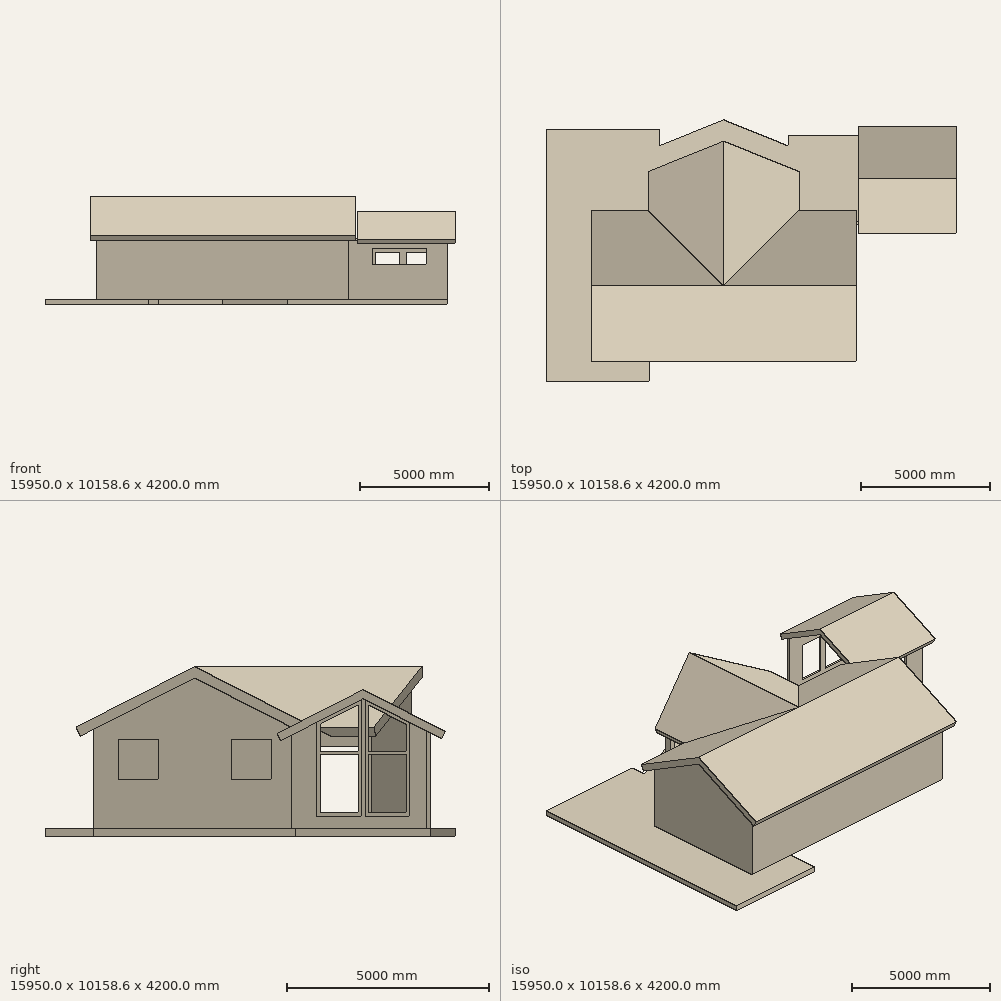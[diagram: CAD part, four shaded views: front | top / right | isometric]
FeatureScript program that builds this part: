
annotation { "Feature Type Name" : "Feature", "Feature Type Description" : "" }
export const myFeature = defineFeature(function(context is Context, id is Id, definition is map)
    precondition{}
    {
        {
            var Q0;
            Q0=qCreatedBy(makeId("Top.planeOp"),FACE);
            var sketch = newSketch(context, id + "F0", { "sketchPlane" : qUnion([Q0])});
            skLineSegment(sketch, "E0", {"start": v(-4900, 0) * mm, "end": v(-4900, 5000) * mm});
            skLineSegment(sketch, "E1", {"start": v(-4900, 5000) * mm, "end": v(-2500, 5000) * mm});
            skLineSegment(sketch, "E2", {"start": v(-2500, 5000) * mm, "end": v(-2500, 6870) * mm});
            skLineSegment(sketch, "E3", {"start": v(-2500, 6870) * mm, "end": v(0, 7880.07) * mm});
            skLineSegment(sketch, "E4", {"start": v(0, 7880.07) * mm, "end": v(2500, 6870) * mm});
            skLineSegment(sketch, "E5", {"start": v(2500, 6870) * mm, "end": v(2500, 5000) * mm});
            skLineSegment(sketch, "E6", {"start": v(2500, 5000) * mm, "end": v(4900, 5000) * mm});
            skLineSegment(sketch, "E7", {"start": v(4900, 5000) * mm, "end": v(4900, 0) * mm});
            skLineSegment(sketch, "E8", {"start": v(4900, 0) * mm, "end": v(-4900, 0) * mm});
            skLineSegment(sketch, "E9", {"start": v(0, 7880.07) * mm, "end": v(-2500, 7880.07) * mm, "construction": true});
            skLineSegment(sketch, "E10", {"start": v(-2500, 7880.07) * mm, "end": v(-2500, 6870) * mm, "construction": true});
            skSolve(sketch);
        }
        {
            var Q0;
            Q0=makeQuery(id+"F0.imprint","IMPRINT",FACE,{"disambiguationData":[TD([[makeQuery(id+"F0.imprint","IMPRINT",EDGE,{"derivedFrom":sQuery(id+"F0.wireOp",EDGE,"E0")}),-1.0]])]});
            extrude(context, id + "F1", {"entities" : qUnion([Q0]), "depth" : 4000 * mm, "offsetDistance" : 25 * mm});
        }
        {
            var Q0;
            Q0=makeQuery(id+"F1.opExtrude","SWEPT_FACE",FACE,{"disambiguationData":[OSD([sQuery(id+"F0.wireOp",EDGE,"E0")])]});
            var sketch = newSketch(context, id + "F2", { "sketchPlane" : qUnion([Q0])});
            skLineSegment(sketch, "E11", {"start": v(-5000, 2726.19) * mm, "end": v(-2500, 4000) * mm});
            skLineSegment(sketch, "E12", {"start": v(-2500, 4000) * mm, "end": v(0, 2726.19) * mm});
            skLineSegment(sketch, "E13", {"start": v(0, 2726.19) * mm, "end": v(0, 4000) * mm});
            skLineSegment(sketch, "E14", {"start": v(0, 4000) * mm, "end": v(-2500, 4000) * mm});
            skLineSegment(sketch, "E15", {"start": v(-5000, 4000) * mm, "end": v(-5000, 2726.19) * mm});
            skSolve(sketch);
        }
        {
            var Q0;
            {var subQ0=sQuery(id+"F2.wireOp",EDGE,"E11");Q0=makeQuery(id+"F2.imprint","IMPRINT",FACE,{"disambiguationData":[TD([[makeQuery(id+"F2.imprint","IMPRINT",EDGE,{"derivedFrom":subQ0}),1.0]])]});}
            var Q1;
            Q1=makeQuery(id+"F2.imprint","IMPRINT",FACE,{"disambiguationData":[TD([[makeQuery(id+"F2.imprint","IMPRINT",EDGE,{"derivedFrom":sQuery(id+"F2.wireOp",EDGE,"E12")}),1.0]])]});
            extrude(context, id + "F3", {"entities" : qUnion([Q0, Q1]), "operationType" : NewBodyOperationType.REMOVE, "endBound" : BoundingType.THROUGH_ALL, "oppositeDirection" : true, "depth" : 25 * mm, "offsetDistance" : 25 * mm});
        }
        {
            var Q0;
            Q0=makeQuery(id+"F3.boolean.opBoolean","COPY",FACE,{"derivedFrom":makeQuery(id+"F3.opExtrude","SWEPT_FACE",FACE,{"disambiguationData":[OSD([sQuery(id+"F2.wireOp",EDGE,"E15")])]})});
            var sketch = newSketch(context, id + "F4", { "sketchPlane" : qUnion([Q0])});
            skLineSegment(sketch, "E16", {"start": v(0, 4000) * mm, "end": v(-2500, 2726.19) * mm});
            skLineSegment(sketch, "E17", {"start": v(-2500, 2726.19) * mm, "end": v(-2500, 4000) * mm});
            skLineSegment(sketch, "E18", {"start": v(-2500, 4000) * mm, "end": v(2500, 4000) * mm});
            skLineSegment(sketch, "E19", {"start": v(2500, 4000) * mm, "end": v(2500, 2726.19) * mm});
            skLineSegment(sketch, "E20", {"start": v(2500, 2726.19) * mm, "end": v(0, 4000) * mm});
            skSolve(sketch);
        }
        {
            var Q0;
            Q0 = qSketchRegion(id + "F4", true);
            extrude(context, id + "F5", {"entities" : qUnion([Q0]), "operationType" : NewBodyOperationType.REMOVE, "endBound" : BoundingType.THROUGH_ALL, "oppositeDirection" : true, "depth" : 25 * mm, "offsetDistance" : 25 * mm});
        }
        {
            var Q0;
            Q0=makeQuery(id+"F1.opExtrude","SWEPT_FACE",FACE,{"disambiguationData":[OSD([sQuery(id+"F0.wireOp",EDGE,"E0")])]});
            var sketch = newSketch(context, id + "F6", { "sketchPlane" : qUnion([Q0])});
            skLineSegment(sketch, "E21", {"start": v(-2500, 4000) * mm, "end": v(-5445.5, 2499.2) * mm});
            skLineSegment(sketch, "E22", {"start": v(-5445.5, 2499.2) * mm, "end": v(-5332, 2276.44) * mm});
            skLineSegment(sketch, "E23", {"start": v(-5332, 2276.44) * mm, "end": v(-2500, 3719.42) * mm});
            skLineSegment(sketch, "E24", {"start": v(-2500, 3719.42) * mm, "end": v(332, 2276.44) * mm});
            skLineSegment(sketch, "E25", {"start": v(332, 2276.44) * mm, "end": v(445.5, 2499.2) * mm});
            skLineSegment(sketch, "E26", {"start": v(445.5, 2499.2) * mm, "end": v(-2500, 4000) * mm});
            skPoint(sketch, "E27", {"position": v(0, 2726.19) * mm});
            skSolve(sketch);
        }
        {
            var Q0;
            Q0 = qSketchRegion(id + "F6", true);
            extrude(context, id + "F7", {"entities" : qUnion([Q0]), "operationType" : NewBodyOperationType.ADD, "depth" : 250 * mm, "offsetDistance" : 25 * mm, "hasSecondDirection" : true, "secondDirectionOppositeDirection" : true, "secondDirectionDepth" : 10050 * mm});
        }
        {
            var Q0;
            Q0=makeQuery(id+"F3.boolean.opBoolean","COPY",FACE,{"derivedFrom":makeQuery(id+"F3.opExtrude","SWEPT_FACE",FACE,{"disambiguationData":[OSD([sQuery(id+"F2.wireOp",EDGE,"E15")])]})});
            var sketch = newSketch(context, id + "F8", { "sketchPlane" : qUnion([Q0])});
            skLineSegment(sketch, "E28", {"start": v(0, 4000) * mm, "end": v(-2945.5, 2499.2) * mm});
            skLineSegment(sketch, "E29", {"start": v(-2945.5, 2499.2) * mm, "end": v(-2832, 2276.44) * mm});
            skLineSegment(sketch, "E30", {"start": v(-2832, 2276.44) * mm, "end": v(0, 3719.42) * mm});
            skLineSegment(sketch, "E31", {"start": v(0, 3719.42) * mm, "end": v(2832, 2276.44) * mm});
            skLineSegment(sketch, "E32", {"start": v(2832, 2276.44) * mm, "end": v(2945.5, 2499.2) * mm});
            skLineSegment(sketch, "E33", {"start": v(2945.5, 2499.2) * mm, "end": v(0, 4000) * mm});
            skPoint(sketch, "E34", {"position": v(-2500, 2726.19) * mm});
            skSolve(sketch);
        }
        {
            var Q0;
            {var subQ5=sQuery(id+"F8.wireOp",EDGE,"E29");Q0=makeQuery(id+"F8.imprint","IMPRINT",FACE,{"disambiguationData":[TD([[makeQuery(id+"F8.imprint","IMPRINT",EDGE,{"derivedFrom":subQ5}),1.0]])]});}
            var Q1;
            {var subQ0=sQuery(id+"F8.wireOp",EDGE,"E33");var subQ1=sQuery(id+"F8.wireOp",EDGE,"E28");var subQ2=makeQuery(id+"F8.imprint","INTERSECT",VERTEX,{"derivedFrom":[subQ1,subQ0]});Q1=makeQuery(id+"F8.imprint","IMPRINT",FACE,{"disambiguationData":[TD([[makeQuery(id+"F8.imprint","IMPRINT",EDGE,{"disambiguationData":[TD([[subQ2,-1.0]])],"derivedFrom":subQ1}),1.0]])]});}
            var Q2;
            {var subQ0=sQuery(id+"F8.wireOp",EDGE,"E32");Q2=makeQuery(id+"F8.imprint","IMPRINT",FACE,{"disambiguationData":[TD([[makeQuery(id+"F8.imprint","IMPRINT",EDGE,{"derivedFrom":subQ0}),1.0]])]});}
            var Q3;
            Q3=makeQuery(id+"F7.boolean.opBoolean","MERGE",FACE,{"derivedFrom":[makeQuery(id+"F3.boolean.opBoolean","COPY",FACE,{"derivedFrom":makeQuery(id+"F3.opExtrude","SWEPT_FACE",FACE,{"disambiguationData":[OSD([sQuery(id+"F2.wireOp",EDGE,"E11")])]})}),makeQuery(id+"F7.opExtrude","SWEPT_FACE",FACE,{"disambiguationData":[OSD([sQuery(id+"F6.wireOp",EDGE,"E21")])]})]});
            extrude(context, id + "F9", {"entities" : qUnion([Q0, Q1, Q2]), "operationType" : NewBodyOperationType.ADD, "oppositeDirection" : true, "depth" : 3130 * mm, "offsetDistance" : 25 * mm, "hasSecondDirection" : true, "secondDirectionBound" : SecondDirectionBoundingType.UP_TO_SURFACE, "secondDirectionOppositeDirection" : false, "secondDirectionDepth" : 25 * mm, "secondDirectionBoundEntityFace" : qUnion([Q3])});
        }
        {
            var Q0;
            Q0=makeQuery(id+"F1.opExtrude","CAP_FACE",FACE,{"disambiguationData":[OSD([sQuery(id+"F0.wireOp",EDGE,"E0"),sQuery(id+"F0.wireOp",EDGE,"E1"),sQuery(id+"F0.wireOp",EDGE,"E2"),sQuery(id+"F0.wireOp",EDGE,"E3"),sQuery(id+"F0.wireOp",EDGE,"E4"),sQuery(id+"F0.wireOp",EDGE,"E5"),sQuery(id+"F0.wireOp",EDGE,"E6"),sQuery(id+"F0.wireOp",EDGE,"E7"),sQuery(id+"F0.wireOp",EDGE,"E8")])],"isStart":true});
            var sketch = newSketch(context, id + "F10", { "sketchPlane" : qUnion([Q0])});
            skLineSegment(sketch, "E35", {"start": v(0, -8130) * mm, "end": v(-2945.5, -6939.94) * mm});
            skLineSegment(sketch, "E36", {"start": v(-2945.5, -6939.94) * mm, "end": v(-2945.5, -8130) * mm});
            skLineSegment(sketch, "E37", {"start": v(-2945.5, -8130) * mm, "end": v(0, -8130) * mm});
            skLineSegment(sketch, "E38", {"start": v(2945.5, -8130) * mm, "end": v(2945.5, -6939.94) * mm});
            skLineSegment(sketch, "E39", {"start": v(2945.5, -6939.94) * mm, "end": v(0, -8130) * mm});
            skLineSegment(sketch, "E40", {"start": v(0, -8130) * mm, "end": v(2945.5, -8130) * mm});
            skSolve(sketch);
        }
        {
            var Q0;
            Q0=makeQuery(id+"F10.imprint","IMPRINT",FACE,{"disambiguationData":[TD([[makeQuery(id+"F10.imprint","IMPRINT",EDGE,{"derivedFrom":sQuery(id+"F10.wireOp",EDGE,"E35")}),1.0]])]});
            var Q1;
            Q1=makeQuery(id+"F10.imprint","IMPRINT",FACE,{"disambiguationData":[TD([[makeQuery(id+"F10.imprint","IMPRINT",EDGE,{"derivedFrom":sQuery(id+"F10.wireOp",EDGE,"E38")}),1.0]])]});
            extrude(context, id + "F11", {"entities" : qUnion([Q0, Q1]), "operationType" : NewBodyOperationType.REMOVE, "endBound" : BoundingType.THROUGH_ALL, "oppositeDirection" : true, "depth" : 25 * mm, "offsetDistance" : 25 * mm});
        }
        {
            var Q0;
            Q0=makeQuery(id+"F1.opExtrude","CAP_FACE",FACE,{"disambiguationData":[OSD([sQuery(id+"F0.wireOp",EDGE,"E0"),sQuery(id+"F0.wireOp",EDGE,"E1"),sQuery(id+"F0.wireOp",EDGE,"E2"),sQuery(id+"F0.wireOp",EDGE,"E3"),sQuery(id+"F0.wireOp",EDGE,"E4"),sQuery(id+"F0.wireOp",EDGE,"E5"),sQuery(id+"F0.wireOp",EDGE,"E6"),sQuery(id+"F0.wireOp",EDGE,"E7"),sQuery(id+"F0.wireOp",EDGE,"E8")])],"isStart":true});
            var sketch = newSketch(context, id + "F12", { "sketchPlane" : qUnion([Q0])});
            skLineSegment(sketch, "E41.0", {"start": v(4700, -4800) * mm, "end": v(4700, -200) * mm});
            skLineSegment(sketch, "E41.1", {"start": v(2300, -4800) * mm, "end": v(4700, -4800) * mm});
            skLineSegment(sketch, "E41.2", {"start": v(4700, -200) * mm, "end": v(-4700, -200) * mm});
            skLineSegment(sketch, "E41.3", {"start": v(2300, -6735.1) * mm, "end": v(2300, -4800) * mm});
            skLineSegment(sketch, "E41.4", {"start": v(0, -7664.36) * mm, "end": v(2300, -6735.1) * mm});
            skLineSegment(sketch, "E41.5", {"start": v(-4700, -200) * mm, "end": v(-4700, -4800) * mm});
            skLineSegment(sketch, "E41.6", {"start": v(-4700, -4800) * mm, "end": v(-2300, -4800) * mm});
            skLineSegment(sketch, "E41.7", {"start": v(-2300, -4800) * mm, "end": v(-2300, -6735.1) * mm});
            skLineSegment(sketch, "E41.8", {"start": v(-2300, -6735.1) * mm, "end": v(0, -7664.36) * mm});
            skLineSegment(sketch, "E42.0", {"start": v(4905, -5005) * mm, "end": v(4905, 5) * mm});
            skLineSegment(sketch, "E42.1", {"start": v(2505, -5005) * mm, "end": v(4905, -5005) * mm});
            skLineSegment(sketch, "E42.2", {"start": v(4905, 5) * mm, "end": v(-4905, 5) * mm});
            skLineSegment(sketch, "E42.3", {"start": v(2505, -6873.37) * mm, "end": v(2505, -5005) * mm});
            skLineSegment(sketch, "E42.4", {"start": v(0, -7885.46) * mm, "end": v(2505, -6873.37) * mm});
            skLineSegment(sketch, "E42.5", {"start": v(-4905, 5) * mm, "end": v(-4905, -5005) * mm});
            skLineSegment(sketch, "E42.6", {"start": v(-4905, -5005) * mm, "end": v(-2505, -5005) * mm});
            skLineSegment(sketch, "E42.7", {"start": v(-2505, -5005) * mm, "end": v(-2505, -6873.37) * mm});
            skLineSegment(sketch, "E42.8", {"start": v(-2505, -6873.37) * mm, "end": v(0, -7885.46) * mm});
            skLineSegment(sketch, "E43", {"start": v(-2300, -4800) * mm, "end": v(2300, -4800) * mm});
            skLineSegment(sketch, "E44", {"start": v(4700, -2500) * mm, "end": v(-4700, -2500) * mm});
            skLineSegment(sketch, "E45", {"start": v(0, -7664.36) * mm, "end": v(0, -4800) * mm});
            skSolve(sketch);
        }
        {
            var Q0;
            Q0=makeQuery(id+"F12.imprint","IMPRINT",FACE,{"disambiguationData":[TD([[makeQuery(id+"F12.imprint","IMPRINT",EDGE,{"derivedFrom":sQuery(id+"F12.wireOp",EDGE,"E41.0")}),1.0]])]});
            var Q1;
            Q1=makeQuery(id+"F7.opExtrude","SWEPT_FACE",FACE,{"disambiguationData":[OSD([sQuery(id+"F6.wireOp",EDGE,"E24")])]});
            extrude(context, id + "F13", {"entities" : qUnion([Q0]), "operationType" : NewBodyOperationType.REMOVE, "endBound" : BoundingType.UP_TO_SURFACE, "oppositeDirection" : true, "depth" : 25 * mm, "endBoundEntityFace" : qUnion([Q1]), "offsetDistance" : 25 * mm});
        }
        {
            var Q0;
            {var subQ3=sQuery(id+"F12.wireOp",EDGE,"E41.1");Q0=makeQuery(id+"F12.imprint","IMPRINT",FACE,{"disambiguationData":[TD([[makeQuery(id+"F12.imprint","IMPRINT",EDGE,{"derivedFrom":subQ3}),1.0]])]});}
            var Q1;
            {var subQ1=sQuery(id+"F6.wireOp",EDGE,"E23");Q1=makeQuery(id+"F7.boolean.opBoolean","SPLIT",FACE,{"disambiguationData":[TD([makeQuery(id+"F1.opExtrude","SWEPT_FACE",FACE,{"disambiguationData":[OSD([sQuery(id+"F0.wireOp",EDGE,"E0")])]})])],"derivedFrom":makeQuery(id+"F7.opExtrude","SWEPT_FACE",FACE,{"disambiguationData":[OSD([subQ1])]})});}
            extrude(context, id + "F14", {"entities" : qUnion([Q0]), "operationType" : NewBodyOperationType.REMOVE, "endBound" : BoundingType.UP_TO_SURFACE, "oppositeDirection" : true, "depth" : 25 * mm, "endBoundEntityFace" : qUnion([Q1]), "offsetDistance" : 25 * mm});
        }
        {
            var Q0;
            {var subQ0=sQuery(id+"F12.wireOp",EDGE,"E41.7");Q0=makeQuery(id+"F12.imprint","IMPRINT",FACE,{"disambiguationData":[TD([[makeQuery(id+"F12.imprint","IMPRINT",EDGE,{"derivedFrom":subQ0}),1.0]])]});}
            var Q1;
            {var subQ1=sQuery(id+"F8.wireOp",EDGE,"E30");Q1=makeQuery(id+"F9.boolean.opBoolean","SPLIT",FACE,{"disambiguationData":[TD([makeQuery(id+"F1.opExtrude","SWEPT_FACE",FACE,{"disambiguationData":[OSD([sQuery(id+"F0.wireOp",EDGE,"E2")])]})])],"derivedFrom":makeQuery(id+"F9.opExtrude","SWEPT_FACE",FACE,{"disambiguationData":[OSD([subQ1])]})});}
            extrude(context, id + "F15", {"entities" : qUnion([Q0]), "operationType" : NewBodyOperationType.REMOVE, "endBound" : BoundingType.UP_TO_SURFACE, "oppositeDirection" : true, "depth" : 25 * mm, "endBoundEntityFace" : qUnion([Q1]), "offsetDistance" : 25 * mm});
        }
        {
            var Q0;
            {var subQ0=sQuery(id+"F12.wireOp",EDGE,"E41.3");Q0=makeQuery(id+"F12.imprint","IMPRINT",FACE,{"disambiguationData":[TD([[makeQuery(id+"F12.imprint","IMPRINT",EDGE,{"derivedFrom":subQ0}),1.0]])]});}
            var Q1;
            {var subQ1=sQuery(id+"F8.wireOp",EDGE,"E31");Q1=makeQuery(id+"F9.boolean.opBoolean","SPLIT",FACE,{"disambiguationData":[TD([makeQuery(id+"F1.opExtrude","SWEPT_FACE",FACE,{"disambiguationData":[OSD([sQuery(id+"F0.wireOp",EDGE,"E3")])]})])],"derivedFrom":makeQuery(id+"F9.opExtrude","SWEPT_FACE",FACE,{"disambiguationData":[OSD([subQ1])]})});}
            extrude(context, id + "F16", {"entities" : qUnion([Q0]), "operationType" : NewBodyOperationType.REMOVE, "endBound" : BoundingType.UP_TO_SURFACE, "oppositeDirection" : true, "depth" : 25 * mm, "endBoundEntityFace" : qUnion([Q1]), "offsetDistance" : 25 * mm});
        }
        {
            var Q0;
            Q0=makeQuery(id+"F1.opExtrude","CAP_FACE",FACE,{"disambiguationData":[OSD([sQuery(id+"F0.wireOp",EDGE,"E0"),sQuery(id+"F0.wireOp",EDGE,"E1"),sQuery(id+"F0.wireOp",EDGE,"E2"),sQuery(id+"F0.wireOp",EDGE,"E3"),sQuery(id+"F0.wireOp",EDGE,"E4"),sQuery(id+"F0.wireOp",EDGE,"E5"),sQuery(id+"F0.wireOp",EDGE,"E6"),sQuery(id+"F0.wireOp",EDGE,"E7"),sQuery(id+"F0.wireOp",EDGE,"E8")])],"isStart":true});
            var sketch = newSketch(context, id + "F17", { "sketchPlane" : qUnion([Q0])});
            skLineSegment(sketch, "E46", {"start": v(-2500, -6870) * mm, "end": v(-2500, -7948.53) * mm});
            skLineSegment(sketch, "E47.0", {"start": v(0, -8958.6) * mm, "end": v(2500, -7948.53) * mm});
            skLineSegment(sketch, "E47.1", {"start": v(-2500, -7948.53) * mm, "end": v(0, -8958.6) * mm});
            skLineSegment(sketch, "E48", {"start": v(2500, -6870) * mm, "end": v(2500, -7948.53) * mm});
            skLineSegment(sketch, "E49.bottom", {"start": v(2500, -5000) * mm, "end": v(8750, -5000) * mm});
            skLineSegment(sketch, "E49.top", {"start": v(2500, -8350) * mm, "end": v(8750, -8350) * mm});
            skLineSegment(sketch, "E49.left", {"start": v(2500, -5000) * mm, "end": v(2500, -8350) * mm});
            skLineSegment(sketch, "E49.right", {"start": v(8750, -5000) * mm, "end": v(8750, -8350) * mm});
            skLineSegment(sketch, "E50.bottom", {"start": v(-2500, -5000) * mm, "end": v(-6900, -5000) * mm});
            skLineSegment(sketch, "E50.top", {"start": v(-2500, -8574.12) * mm, "end": v(-6900, -8574.12) * mm});
            skLineSegment(sketch, "E50.left", {"start": v(-2500, -5000) * mm, "end": v(-2500, -8574.12) * mm});
            skLineSegment(sketch, "E50.right", {"start": v(-6900, -5000) * mm, "end": v(-6900, -8574.12) * mm});
            skLineSegment(sketch, "E51.bottom", {"start": v(-6900, -5000) * mm, "end": v(-4900, -5000) * mm});
            skLineSegment(sketch, "E51.top", {"start": v(-6900, 1200) * mm, "end": v(-4900, 1200) * mm});
            skLineSegment(sketch, "E51.left", {"start": v(-6900, -5000) * mm, "end": v(-6900, 1200) * mm});
            skLineSegment(sketch, "E51.right", {"start": v(-4900, -5000) * mm, "end": v(-4900, 1200) * mm});
            skLineSegment(sketch, "E52.bottom", {"start": v(-4900, 1200) * mm, "end": v(-2900, 1200) * mm});
            skLineSegment(sketch, "E52.top", {"start": v(-4900, 0) * mm, "end": v(-2900, 0) * mm});
            skLineSegment(sketch, "E52.left", {"start": v(-4900, 1200) * mm, "end": v(-4900, 0) * mm});
            skLineSegment(sketch, "E52.right", {"start": v(-2900, 1200) * mm, "end": v(-2900, 0) * mm});
            skSolve(sketch);
        }
        {
            var Q0;
            {var subQ2=sQuery(id+"F17.wireOp",EDGE,"E52.bottom");Q0=makeQuery(id+"F17.imprint","IMPRINT",FACE,{"disambiguationData":[TD([[makeQuery(id+"F17.imprint","IMPRINT",EDGE,{"derivedFrom":subQ2}),-1.0]])]});}
            var Q1;
            {var subQ4=sQuery(id+"F17.wireOp",EDGE,"E46");Q1=makeQuery(id+"F17.imprint","IMPRINT",FACE,{"disambiguationData":[TD([[makeQuery(id+"F17.imprint","IMPRINT",EDGE,{"derivedFrom":subQ4}),-1.0]])]});}
            var Q2;
            {var subQ5=sQuery(id+"F17.wireOp",EDGE,"E51.top");Q2=makeQuery(id+"F17.imprint","IMPRINT",FACE,{"disambiguationData":[TD([[makeQuery(id+"F17.imprint","IMPRINT",EDGE,{"derivedFrom":subQ5}),-1.0]])]});}
            var Q3;
            Q3=makeQuery(id+"F17.imprint","IMPRINT",FACE,{"disambiguationData":[TD([[makeQuery(id+"F17.imprint","IMPRINT",EDGE,{"derivedFrom":sQuery(id+"F17.wireOp",EDGE,"E46")}),1.0]])]});
            var Q4;
            {var subQ6=sQuery(id+"F17.wireOp",EDGE,"E48");Q4=makeQuery(id+"F17.imprint","IMPRINT",FACE,{"disambiguationData":[TD([[makeQuery(id+"F17.imprint","IMPRINT",EDGE,{"derivedFrom":subQ6}),1.0]])]});}
            extrude(context, id + "F18", {"entities" : qUnion([Q0, Q1, Q2, Q3, Q4]), "depth" : 200 * mm, "offsetDistance" : 25 * mm});
        }
        {
            var Q0;
            Q0=makeQuery(id+"F1.opExtrude","SWEPT_FACE",FACE,{"disambiguationData":[OSD([sQuery(id+"F0.wireOp",EDGE,"E3")])]});
            var sketch = newSketch(context, id + "F19", { "sketchPlane" : qUnion([Q0])});
            skLineSegment(sketch, "E53.bottom", {"start": v(-2801.92, 300) * mm, "end": v(-1778.76, 300) * mm});
            skLineSegment(sketch, "E53.top", {"start": v(-2801.92, 2027.36) * mm, "end": v(-1778.76, 2027.36) * mm});
            skLineSegment(sketch, "E53.left", {"start": v(-2801.92, 300) * mm, "end": v(-2801.92, 2027.36) * mm});
            skLineSegment(sketch, "E53.right", {"start": v(-1778.76, 300) * mm, "end": v(-1778.76, 2027.36) * mm});
            skLineSegment(sketch, "E54.bottom", {"start": v(-1578.76, 2027.36) * mm, "end": v(-555.59, 2027.36) * mm});
            skLineSegment(sketch, "E54.top", {"start": v(-1578.76, 300) * mm, "end": v(-555.59, 300) * mm});
            skLineSegment(sketch, "E54.left", {"start": v(-1578.76, 2027.36) * mm, "end": v(-1578.76, 300) * mm});
            skLineSegment(sketch, "E54.right", {"start": v(-555.59, 2027.36) * mm, "end": v(-555.59, 300) * mm});
            skLineSegment(sketch, "E55", {"start": v(-2801.92, 2227.36) * mm, "end": v(-2801.92, 3427.36) * mm});
            skLineSegment(sketch, "E56", {"start": v(-2801.92, 3427.36) * mm, "end": v(-1778.76, 2944) * mm});
            skLineSegment(sketch, "E57", {"start": v(-1778.76, 2944) * mm, "end": v(-1778.76, 2227.36) * mm});
            skLineSegment(sketch, "E58", {"start": v(-1778.76, 2227.36) * mm, "end": v(-2801.92, 2227.36) * mm});
            skLineSegment(sketch, "E59", {"start": v(-1578.76, 2227.36) * mm, "end": v(-1578.76, 2849.5) * mm});
            skLineSegment(sketch, "E60", {"start": v(-1578.76, 2849.5) * mm, "end": v(-555.59, 2366.14) * mm});
            skLineSegment(sketch, "E61", {"start": v(-555.59, 2366.14) * mm, "end": v(-555.59, 2227.36) * mm});
            skLineSegment(sketch, "E62", {"start": v(-555.59, 2227.36) * mm, "end": v(-1578.76, 2227.36) * mm});
            skSolve(sketch);
        }
        {
            var Q0;
            Q0=makeQuery(id+"F19.imprint","IMPRINT",FACE,{"disambiguationData":[TD([[makeQuery(id+"F19.imprint","IMPRINT",EDGE,{"derivedFrom":sQuery(id+"F19.wireOp",EDGE,"E55")}),-1.0]])]});
            var Q1;
            Q1=makeQuery(id+"F19.imprint","IMPRINT",FACE,{"disambiguationData":[TD([[makeQuery(id+"F19.imprint","IMPRINT",EDGE,{"derivedFrom":sQuery(id+"F19.wireOp",EDGE,"E53.bottom")}),1.0]])]});
            var Q2;
            Q2=makeQuery(id+"F19.imprint","IMPRINT",FACE,{"disambiguationData":[TD([[makeQuery(id+"F19.imprint","IMPRINT",EDGE,{"derivedFrom":sQuery(id+"F19.wireOp",EDGE,"E54.bottom")}),-1.0]])]});
            var Q3;
            Q3=makeQuery(id+"F19.imprint","IMPRINT",FACE,{"disambiguationData":[TD([[makeQuery(id+"F19.imprint","IMPRINT",EDGE,{"derivedFrom":sQuery(id+"F19.wireOp",EDGE,"E59")}),-1.0]])]});
            extrude(context, id + "F20", {"entities" : qUnion([Q0, Q1, Q2, Q3]), "operationType" : NewBodyOperationType.REMOVE, "oppositeDirection" : true, "depth" : 500 * mm, "offsetDistance" : 25 * mm});
        }
        {
            var Q0;
            Q0=makeQuery(id+"F1.opExtrude","SWEPT_FACE",FACE,{"disambiguationData":[OSD([sQuery(id+"F0.wireOp",EDGE,"E2")])]});
            var sketch = newSketch(context, id + "F21", { "sketchPlane" : qUnion([Q0])});
            skLineSegment(sketch, "E63.bottom", {"start": v(-5617.69, 300) * mm, "end": v(-6617.69, 300) * mm});
            skLineSegment(sketch, "E63.top", {"start": v(-5617.69, 2027.36) * mm, "end": v(-6617.69, 2027.36) * mm});
            skLineSegment(sketch, "E63.left", {"start": v(-5617.69, 300) * mm, "end": v(-5617.69, 2027.36) * mm});
            skLineSegment(sketch, "E63.right", {"start": v(-6617.69, 300) * mm, "end": v(-6617.69, 2027.36) * mm});
            skSolve(sketch);
        }
        {
            var Q0;
            Q0 = qSketchRegion(id + "F21", true);
            extrude(context, id + "F22", {"entities" : qUnion([Q0]), "operationType" : NewBodyOperationType.REMOVE, "endBound" : BoundingType.THROUGH_ALL, "oppositeDirection" : true, "depth" : 25 * mm, "offsetDistance" : 25 * mm});
        }
        {
            var Q0;
            Q0=makeQuery(id+"F1.opExtrude","SWEPT_FACE",FACE,{"disambiguationData":[OSD([sQuery(id+"F0.wireOp",EDGE,"E6")])]});
            var sketch = newSketch(context, id + "F23", { "sketchPlane" : qUnion([Q0])});
            skLineSegment(sketch, "E64.bottom", {"start": v(-2877.21, 133.01) * mm, "end": v(-3677.21, 133.01) * mm});
            skLineSegment(sketch, "E64.top", {"start": v(-2877.21, 2133.01) * mm, "end": v(-3677.21, 2133.01) * mm});
            skLineSegment(sketch, "E64.left", {"start": v(-2877.21, 133.01) * mm, "end": v(-2877.21, 2133.01) * mm});
            skLineSegment(sketch, "E64.right", {"start": v(-3677.21, 133.01) * mm, "end": v(-3677.21, 2133.01) * mm});
            skLineSegment(sketch, "E65.bottom", {"start": v(3800, 2133.01) * mm, "end": v(4300, 2133.01) * mm});
            skLineSegment(sketch, "E65.top", {"start": v(3800, 1133.01) * mm, "end": v(4300, 1133.01) * mm});
            skLineSegment(sketch, "E65.left", {"start": v(3800, 2133.01) * mm, "end": v(3800, 1133.01) * mm});
            skLineSegment(sketch, "E65.right", {"start": v(4300, 2133.01) * mm, "end": v(4300, 1133.01) * mm});
            skSolve(sketch);
        }
        {
            var Q0;
            Q0=makeQuery(id+"F23.imprint","IMPRINT",FACE,{"disambiguationData":[TD([[makeQuery(id+"F23.imprint","IMPRINT",EDGE,{"derivedFrom":sQuery(id+"F23.wireOp",EDGE,"E64.bottom")}),-1.0]])]});
            var Q1;
            Q1=makeQuery(id+"F23.imprint","IMPRINT",FACE,{"disambiguationData":[TD([[makeQuery(id+"F23.imprint","IMPRINT",EDGE,{"derivedFrom":sQuery(id+"F23.wireOp",EDGE,"E65.bottom")}),-1.0]])]});
            extrude(context, id + "F24", {"entities" : qUnion([Q0, Q1]), "operationType" : NewBodyOperationType.REMOVE, "oppositeDirection" : true, "depth" : 500 * mm, "offsetDistance" : 25 * mm});
        }
        {
            var Q0;
            Q0=makeQuery(id+"F1.opExtrude","SWEPT_FACE",FACE,{"disambiguationData":[OSD([sQuery(id+"F0.wireOp",EDGE,"E7")])]});
            var sketch = newSketch(context, id + "F25", { "sketchPlane" : qUnion([Q0])});
            skLineSegment(sketch, "E66.bottom", {"start": v(600, 2200) * mm, "end": v(1600, 2200) * mm});
            skLineSegment(sketch, "E66.top", {"start": v(600, 1200) * mm, "end": v(1600, 1200) * mm});
            skLineSegment(sketch, "E66.left", {"start": v(600, 2200) * mm, "end": v(600, 1200) * mm});
            skLineSegment(sketch, "E66.right", {"start": v(1600, 2200) * mm, "end": v(1600, 1200) * mm});
            skLineSegment(sketch, "E67.bottom", {"start": v(3400, 2200) * mm, "end": v(4400, 2200) * mm});
            skLineSegment(sketch, "E67.top", {"start": v(3400, 1200) * mm, "end": v(4400, 1200) * mm});
            skLineSegment(sketch, "E67.left", {"start": v(3400, 2200) * mm, "end": v(3400, 1200) * mm});
            skLineSegment(sketch, "E67.right", {"start": v(4400, 2200) * mm, "end": v(4400, 1200) * mm});
            skSolve(sketch);
        }
        {
            var Q0;
            Q0 = qSketchRegion(id + "F25", true);
            extrude(context, id + "F26", {"entities" : qUnion([Q0]), "operationType" : NewBodyOperationType.REMOVE, "oppositeDirection" : true, "depth" : 500 * mm, "offsetDistance" : 25 * mm});
        }
        {
            var Q0;
            Q0=makeQuery(id+"F18.opExtrude","SWEPT_FACE",FACE,{"disambiguationData":[OSD([sQuery(id+"F17.wireOp",EDGE,"E49.right")])]});
            var sketch = newSketch(context, id + "F27", { "sketchPlane" : qUnion([Q0])});
            skLineSegment(sketch, "E68", {"start": v(5525, 300) * mm, "end": v(5525, 2619.52) * mm});
            skLineSegment(sketch, "E69", {"start": v(5525, 2619.52) * mm, "end": v(6625, 3180) * mm});
            skLineSegment(sketch, "E70", {"start": v(6625, 3180) * mm, "end": v(6625, 300) * mm});
            skLineSegment(sketch, "E71", {"start": v(6625, 300) * mm, "end": v(5525, 300) * mm});
            skLineSegment(sketch, "E72", {"start": v(6725, 3180) * mm, "end": v(7825, 2619.52) * mm});
            skLineSegment(sketch, "E73", {"start": v(7825, 2619.52) * mm, "end": v(7825, 300) * mm});
            skLineSegment(sketch, "E74", {"start": v(7825, 300) * mm, "end": v(6725, 300) * mm});
            skLineSegment(sketch, "E75", {"start": v(6725, 300) * mm, "end": v(6725, 3180) * mm});
            skLineSegment(sketch, "E76", {"start": v(6625, 300) * mm, "end": v(6725, 300) * mm, "construction": true});
            skLineSegment(sketch, "E77", {"start": v(6675, 300) * mm, "end": v(6675, 0) * mm, "construction": true});
            skLineSegment(sketch, "E78.0", {"start": v(5605, 2570.5) * mm, "end": v(6545, 3049.45) * mm});
            skLineSegment(sketch, "E78.1", {"start": v(5605, 380) * mm, "end": v(5605, 2570.5) * mm});
            skLineSegment(sketch, "E78.2", {"start": v(6545, 380) * mm, "end": v(5605, 380) * mm});
            skLineSegment(sketch, "E78.3", {"start": v(6545, 3049.45) * mm, "end": v(6545, 380) * mm});
            skLineSegment(sketch, "E79.0", {"start": v(6805, 380) * mm, "end": v(6805, 3049.45) * mm});
            skLineSegment(sketch, "E79.1", {"start": v(7745, 380) * mm, "end": v(6805, 380) * mm});
            skLineSegment(sketch, "E79.2", {"start": v(7745, 2570.5) * mm, "end": v(7745, 380) * mm});
            skLineSegment(sketch, "E79.3", {"start": v(6805, 3049.45) * mm, "end": v(7745, 2570.5) * mm});
            skLineSegment(sketch, "E80", {"start": v(5605, 1900) * mm, "end": v(6545, 1900) * mm});
            skLineSegment(sketch, "E81", {"start": v(7745, 1820) * mm, "end": v(6805, 1820) * mm});
            skLineSegment(sketch, "E82.trimOffspring", {"start": v(6805, 1900) * mm, "end": v(7745, 1900) * mm});
            skLineSegment(sketch, "E83.trimOffspring", {"start": v(6545, 1820) * mm, "end": v(5605, 1820) * mm});
            skLineSegment(sketch, "E84", {"start": v(6675, 3429.94) * mm, "end": v(4541.9, 2343.07) * mm});
            skLineSegment(sketch, "E85", {"start": v(5000, 2352.02) * mm, "end": v(5000, 0) * mm});
            skLineSegment(sketch, "E86", {"start": v(5000, 0) * mm, "end": v(8350, 0) * mm});
            skLineSegment(sketch, "E87", {"start": v(8350, 0) * mm, "end": v(8350, 2352.02) * mm});
            skLineSegment(sketch, "E88", {"start": v(8708.1, 2394.03) * mm, "end": v(6675, 3429.94) * mm});
            skLineSegment(sketch, "E89", {"start": v(5525, 2619.52) * mm, "end": v(4632.7, 2164.87) * mm});
            skLineSegment(sketch, "E90", {"start": v(7825, 2619.52) * mm, "end": v(8617.3, 2215.82) * mm});
            skLineSegment(sketch, "E91", {"start": v(4900, 0) * mm, "end": v(4900, 2301.07) * mm});
            skLineSegment(sketch, "E92", {"start": v(8250, 0) * mm, "end": v(8250, 2402.97) * mm});
            skLineSegment(sketch, "E93", {"start": v(4900, 0) * mm, "end": v(5000, 0) * mm});
            skLineSegment(sketch, "E94", {"start": v(4541.9, 2343.07) * mm, "end": v(4632.7, 2164.87) * mm});
            skPoint(sketch, "E95", {"position": v(4900, 2301.07) * mm});
            skLineSegment(sketch, "E96", {"start": v(8617.3, 2215.82) * mm, "end": v(8708.1, 2394.03) * mm});
            skPoint(sketch, "E97.orphan", {"position": v(8350, 2352.02) * mm});
            skLineSegment(sketch, "E98", {"start": v(6625, 3180) * mm, "end": v(6675, 3205.48) * mm});
            skLineSegment(sketch, "E99", {"start": v(6675, 3205.48) * mm, "end": v(6725, 3180) * mm});
            skLineSegment(sketch, "E100", {"start": v(5605, 2041.05) * mm, "end": v(6545, 2520) * mm});
            skLineSegment(sketch, "E101", {"start": v(6805, 2520) * mm, "end": v(7745, 2041.05) * mm});
            skSolve(sketch);
        }
        {
            var Q0;
            {var subQ4=sQuery(id+"F27.wireOp",EDGE,"E68");Q0=makeQuery(id+"F27.imprint","IMPRINT",FACE,{"disambiguationData":[TD([[makeQuery(id+"F27.imprint","IMPRINT",EDGE,{"derivedFrom":subQ4}),1.0]])]});}
            var Q1;
            Q1=makeQuery(id+"F27.imprint","IMPRINT",FACE,{"disambiguationData":[TD([[makeQuery(id+"F27.imprint","IMPRINT",EDGE,{"derivedFrom":sQuery(id+"F27.wireOp",EDGE,"E72")}),-1.0]])]});
            var Q2;
            Q2=makeQuery(id+"F27.imprint","IMPRINT",FACE,{"disambiguationData":[TD([[makeQuery(id+"F27.imprint","IMPRINT",EDGE,{"derivedFrom":sQuery(id+"F27.wireOp",EDGE,"E68")}),-1.0]])]});
            var Q3;
            {var subQ0=sQuery(id+"F27.wireOp",EDGE,"E81");Q3=makeQuery(id+"F27.imprint","IMPRINT",FACE,{"disambiguationData":[TD([[makeQuery(id+"F27.imprint","IMPRINT",EDGE,{"derivedFrom":subQ0}),-1.0]])]});}
            var Q4;
            {var subQ0=sQuery(id+"F27.wireOp",EDGE,"E80");Q4=makeQuery(id+"F27.imprint","IMPRINT",FACE,{"disambiguationData":[TD([[makeQuery(id+"F27.imprint","IMPRINT",EDGE,{"derivedFrom":subQ0}),-1.0]])]});}
            extrude(context, id + "F28", {"entities" : qUnion([Q0, Q1, Q2, Q3, Q4]), "oppositeDirection" : true, "depth" : 100 * mm, "offsetDistance" : 25 * mm});
        }
        {
            var Q0;
            {var subQ0=sQuery(id+"F27.wireOp",EDGE,"E80");Q0=makeQuery(id+"F27.imprint","IMPRINT",FACE,{"disambiguationData":[TD([[makeQuery(id+"F27.imprint","IMPRINT",EDGE,{"derivedFrom":subQ0}),-1.0]])]});}
            var Q1;
            Q1=makeQuery(id+"F27.imprint","IMPRINT",FACE,{"disambiguationData":[TD([[makeQuery(id+"F27.imprint","IMPRINT",EDGE,{"derivedFrom":sQuery(id+"F27.wireOp",EDGE,"E68")}),-1.0]])]});
            var Q2;
            Q2=makeQuery(id+"F27.imprint","IMPRINT",FACE,{"disambiguationData":[TD([[makeQuery(id+"F27.imprint","IMPRINT",EDGE,{"derivedFrom":sQuery(id+"F27.wireOp",EDGE,"E72")}),-1.0]])]});
            var Q3;
            {var subQ0=sQuery(id+"F27.wireOp",EDGE,"E81");Q3=makeQuery(id+"F27.imprint","IMPRINT",FACE,{"disambiguationData":[TD([[makeQuery(id+"F27.imprint","IMPRINT",EDGE,{"derivedFrom":subQ0}),-1.0]])]});}
            extrude(context, id + "F29", {"entities" : qUnion([Q0, Q1, Q2, Q3]), "operationType" : NewBodyOperationType.REMOVE, "oppositeDirection" : true, "depth" : 25 * mm, "offsetDistance" : 25 * mm});
        }
        {
            var Q0;
            {var subQ0=sQuery(id+"F27.wireOp",EDGE,"E85");Q0=makeQuery(id+"F27.imprint","IMPRINT",FACE,{"disambiguationData":[TD([[makeQuery(id+"F27.imprint","IMPRINT",EDGE,{"derivedFrom":subQ0}),-1.0]])]});}
            var Q1;
            Q1=makeQuery(id+"F1.opExtrude","SWEPT_FACE",FACE,{"disambiguationData":[OSD([sQuery(id+"F0.wireOp",EDGE,"E7")])]});
            extrude(context, id + "F30", {"entities" : qUnion([Q0]), "endBound" : BoundingType.UP_TO_SURFACE, "oppositeDirection" : true, "depth" : 25 * mm, "endBoundEntityFace" : qUnion([Q1]), "offsetDistance" : 25 * mm});
        }
        {
            var Q0;
            {var subQ7=sQuery(id+"F27.wireOp",EDGE,"E69");Q0=makeQuery(id+"F27.imprint","IMPRINT",FACE,{"disambiguationData":[TD([[makeQuery(id+"F27.imprint","IMPRINT",EDGE,{"derivedFrom":subQ7}),1.0]])]});}
            var Q1;
            Q1=makeQuery(id+"F1.opExtrude","SWEPT_FACE",FACE,{"disambiguationData":[OSD([sQuery(id+"F0.wireOp",EDGE,"E7")])]});
            extrude(context, id + "F31", {"entities" : qUnion([Q0]), "operationType" : NewBodyOperationType.ADD, "depth" : 300 * mm, "endBoundEntityFace" : qUnion([Q1]), "offsetDistance" : 25 * mm, "hasSecondDirection" : true, "secondDirectionOppositeDirection" : true, "secondDirectionDepth" : 3500 * mm});
        }
        {
            var Q0;
            {var subQ0=sQuery(id+"F27.wireOp",EDGE,"E87");Q0=makeQuery(id+"F27.imprint","IMPRINT",FACE,{"disambiguationData":[TD([[makeQuery(id+"F27.imprint","IMPRINT",EDGE,{"derivedFrom":subQ0}),1.0]])]});}
            extrude(context, id + "F32", {"entities" : qUnion([Q0]), "oppositeDirection" : true, "depth" : 3500 * mm, "offsetDistance" : 25 * mm});
        }
        {
            var Q0;
            Q0=makeQuery(id+"F18.opExtrude","SWEPT_FACE",FACE,{"disambiguationData":[OSD([sQuery(id+"F17.wireOp",EDGE,"E49.top")])]});
            var sketch = newSketch(context, id + "F33", { "sketchPlane" : qUnion([Q0])});
            skLineSegment(sketch, "E102.bottom", {"start": v(-8145, 300) * mm, "end": v(-7045, 300) * mm});
            skLineSegment(sketch, "E102.top", {"start": v(-8145, 1900) * mm, "end": v(-7045, 1900) * mm});
            skLineSegment(sketch, "E102.left", {"start": v(-8145, 300) * mm, "end": v(-8145, 1900) * mm});
            skLineSegment(sketch, "E102.right", {"start": v(-7045, 300) * mm, "end": v(-7045, 1900) * mm});
            skLineSegment(sketch, "E103.0", {"start": v(-8065, 1820) * mm, "end": v(-7125, 1820) * mm});
            skLineSegment(sketch, "E103.1", {"start": v(-8065, 380) * mm, "end": v(-8065, 1820) * mm});
            skLineSegment(sketch, "E103.2", {"start": v(-8065, 380) * mm, "end": v(-7125, 380) * mm});
            skLineSegment(sketch, "E103.3", {"start": v(-7125, 380) * mm, "end": v(-7125, 1820) * mm});
            skLineSegment(sketch, "E104.0", {"start": v(-8745, 2347.02) * mm, "end": v(-8745, 5) * mm});
            skLineSegment(sketch, "E104.1", {"start": v(-5255, 2347.02) * mm, "end": v(-8745, 2347.02) * mm});
            skLineSegment(sketch, "E104.2", {"start": v(-5255, 5) * mm, "end": v(-5255, 2347.02) * mm});
            skLineSegment(sketch, "E104.3", {"start": v(-8745, 5) * mm, "end": v(-5255, 5) * mm});
            skLineSegment(sketch, "E105.1.0.0", {"start": v(-5925, 380) * mm, "end": v(-5925, 1820) * mm});
            skLineSegment(sketch, "E105.1.0.1", {"start": v(-6865, 1820) * mm, "end": v(-5925, 1820) * mm});
            skLineSegment(sketch, "E105.1.0.2", {"start": v(-6865, 380) * mm, "end": v(-6865, 1820) * mm});
            skLineSegment(sketch, "E105.1.0.3", {"start": v(-6865, 380) * mm, "end": v(-5925, 380) * mm});
            skLineSegment(sketch, "E105.1.0.4", {"start": v(-6945, 300) * mm, "end": v(-6945, 1900) * mm});
            skLineSegment(sketch, "E105.1.0.5", {"start": v(-5845, 300) * mm, "end": v(-5845, 1900) * mm});
            skLineSegment(sketch, "E105.1.0.6", {"start": v(-6945, 300) * mm, "end": v(-5845, 300) * mm});
            skLineSegment(sketch, "E105.1.0.7", {"start": v(-6945, 1900) * mm, "end": v(-5845, 1900) * mm});
            skLineSegment(sketch, "E105.2.0.0", {"start": v(-4725, 380) * mm, "end": v(-4725, 1820) * mm, "construction": true});
            skLineSegment(sketch, "E105.2.0.1", {"start": v(-5665, 1820) * mm, "end": v(-4725, 1820) * mm, "construction": true});
            skLineSegment(sketch, "E105.2.0.2", {"start": v(-5665, 380) * mm, "end": v(-5665, 1820) * mm, "construction": true});
            skLineSegment(sketch, "E105.2.0.3", {"start": v(-5665, 380) * mm, "end": v(-4725, 380) * mm, "construction": true});
            skLineSegment(sketch, "E105.2.0.4", {"start": v(-5745, 300) * mm, "end": v(-5745, 1900) * mm, "construction": true});
            skLineSegment(sketch, "E105.2.0.5", {"start": v(-4645, 300) * mm, "end": v(-4645, 1900) * mm, "construction": true});
            skLineSegment(sketch, "E105.2.0.6", {"start": v(-5745, 300) * mm, "end": v(-4645, 300) * mm, "construction": true});
            skLineSegment(sketch, "E105.2.0.7", {"start": v(-5745, 1900) * mm, "end": v(-4645, 1900) * mm, "construction": true});
            skLineSegment(sketch, "E105.direction1", {"start": v(-8145, 300) * mm, "end": v(-6945, 300) * mm, "construction": true});
            skSolve(sketch);
        }
        {
            var Q0;
            Q0=makeQuery(id+"F33.imprint","IMPRINT",FACE,{"disambiguationData":[TD([[makeQuery(id+"F33.imprint","IMPRINT",EDGE,{"derivedFrom":sQuery(id+"F33.wireOp",EDGE,"E103.0")}),-1.0]])]});
            var Q1;
            Q1=makeQuery(id+"F33.imprint","IMPRINT",FACE,{"disambiguationData":[TD([[makeQuery(id+"F33.imprint","IMPRINT",EDGE,{"derivedFrom":sQuery(id+"F33.wireOp",EDGE,"E105.1.0.0")}),1.0]])]});
            var Q2;
            Q2=makeQuery(id+"F33.imprint","IMPRINT",FACE,{"disambiguationData":[TD([[makeQuery(id+"F33.imprint","IMPRINT",EDGE,{"derivedFrom":sQuery(id+"F33.wireOp",EDGE,"E105.2.0.0")}),1.0]])]});
            extrude(context, id + "F34", {"entities" : qUnion([Q0, Q1, Q2]), "operationType" : NewBodyOperationType.REMOVE, "endBound" : BoundingType.UP_TO_NEXT, "oppositeDirection" : true, "depth" : 25 * mm, "offsetDistance" : 25 * mm});
        }
        {
            var Q0;
            {var subQ1=sQuery(id+"F33.wireOp",EDGE,"E102.bottom");Q0=makeQuery(id+"F33.imprint","IMPRINT",FACE,{"disambiguationData":[TD([[makeQuery(id+"F33.imprint","IMPRINT",EDGE,{"derivedFrom":subQ1}),1.0]])]});}
            var Q1;
            Q1=makeQuery(id+"F33.imprint","IMPRINT",FACE,{"disambiguationData":[TD([[makeQuery(id+"F33.imprint","IMPRINT",EDGE,{"derivedFrom":sQuery(id+"F33.wireOp",EDGE,"E105.1.0.0")}),-1.0]])]});
            var Q2;
            Q2=makeQuery(id+"F33.imprint","IMPRINT",FACE,{"disambiguationData":[TD([[makeQuery(id+"F33.imprint","IMPRINT",EDGE,{"derivedFrom":sQuery(id+"F33.wireOp",EDGE,"E105.2.0.0")}),-1.0]])]});
            extrude(context, id + "F35", {"entities" : qUnion([Q0, Q1, Q2]), "operationType" : NewBodyOperationType.REMOVE, "oppositeDirection" : true, "depth" : 25 * mm, "offsetDistance" : 25 * mm});
        }
        {
            var Q0;
            Q0=makeQuery(id+"F30.opExtrude","SWEPT_FACE",FACE,{"disambiguationData":[OSD([sQuery(id+"F27.wireOp",EDGE,"E91")])]});
            var sketch = newSketch(context, id + "F36", { "sketchPlane" : qUnion([Q0])});
            skLineSegment(sketch, "E106.bottom", {"start": v(5820.16, 1986.08) * mm, "end": v(7913.5, 1986.08) * mm});
            skLineSegment(sketch, "E106.top", {"start": v(5820.16, 1352) * mm, "end": v(7913.5, 1352) * mm});
            skLineSegment(sketch, "E106.left", {"start": v(5820.16, 1986.08) * mm, "end": v(5820.16, 1352) * mm});
            skLineSegment(sketch, "E106.right", {"start": v(7913.5, 1986.08) * mm, "end": v(7913.5, 1352) * mm});
            skLineSegment(sketch, "E107", {"start": v(6866.83, 1986.08) * mm, "end": v(6866.83, 1352) * mm, "construction": true});
            skLineSegment(sketch, "E108", {"start": v(6736.83, 1352) * mm, "end": v(6736.83, 1986.08) * mm});
            skLineSegment(sketch, "E109", {"start": v(6996.83, 1986.08) * mm, "end": v(6996.83, 1352) * mm});
            skLineSegment(sketch, "E110", {"start": v(6866.83, 1669.04) * mm, "end": v(6996.83, 1669.04) * mm, "construction": true});
            skLineSegment(sketch, "E111", {"start": v(6866.83, 1669.04) * mm, "end": v(6736.83, 1669.04) * mm, "construction": true});
            skSolve(sketch);
        }
        {
            var Q0;
            Q0=makeQuery(id+"F36.imprint","IMPRINT",FACE,{"disambiguationData":[TD([[makeQuery(id+"F36.imprint","IMPRINT",EDGE,{"derivedFrom":sQuery(id+"F36.wireOp",EDGE,"E106.bottom")}),-1.0]])]});
            extrude(context, id + "F37", {"entities" : qUnion([Q0]), "operationType" : NewBodyOperationType.REMOVE, "oppositeDirection" : true, "depth" : 100 * mm, "offsetDistance" : 25 * mm});
        }
    });
